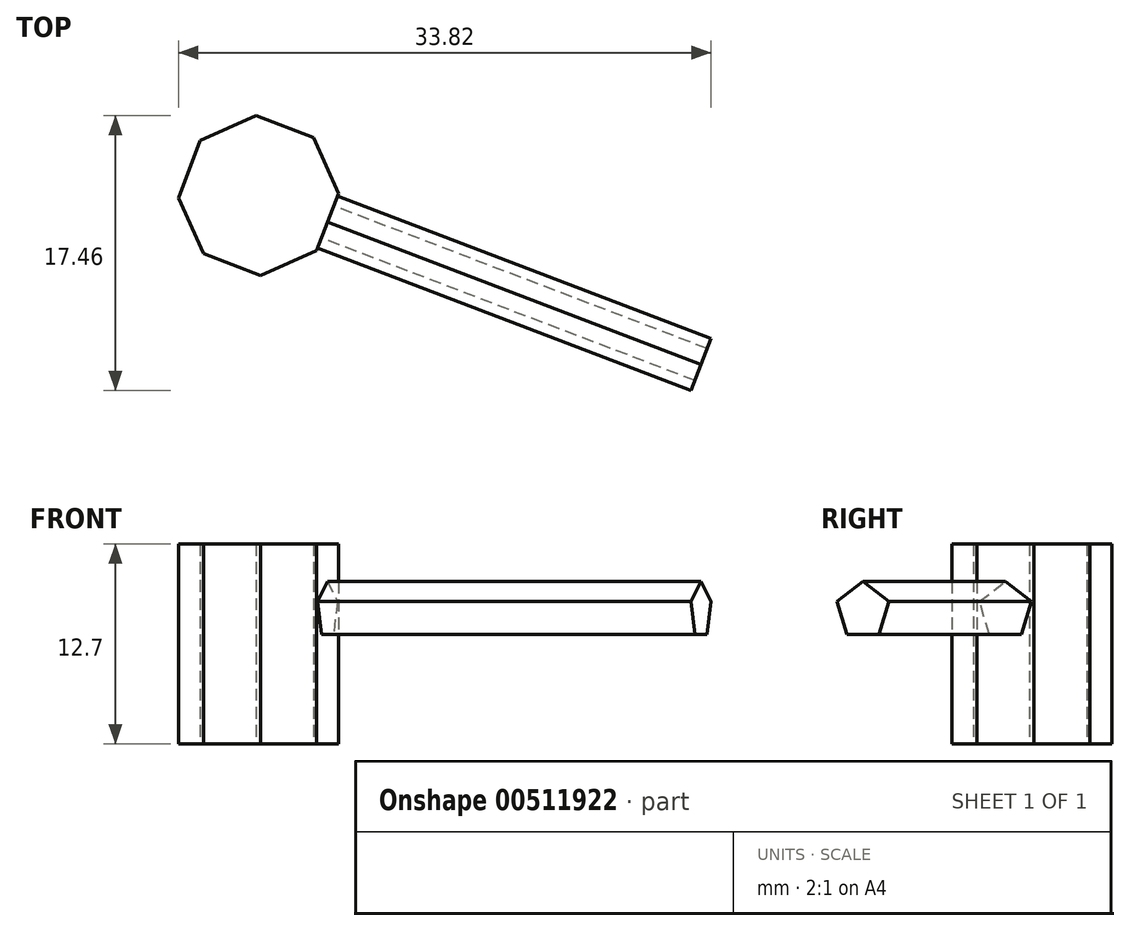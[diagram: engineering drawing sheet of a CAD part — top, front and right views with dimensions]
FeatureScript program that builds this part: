
annotation { "Feature Type Name" : "Feature", "Feature Type Description" : "" }
export const myFeature = defineFeature(function(context is Context, id is Id, definition is map)
    precondition{}
    {
        {
            var Q0;
            Q0=qCreatedBy(makeId("Top.planeOp"),FACE);
            var sketch = newSketch(context, id + "F0", { "sketchPlane" : qUnion([Q0])});
            skCircle(sketch, "E0", {"center": v(0, 0) * mm, "radius": 25.4 * mm});
            skCircle(sketch, "E1.cCircle", {"center": v(0, 0) * mm, "radius": 4.7 * mm, "construction": true});
            skLineSegment(sketch, "E1.0", {"start": v(-3.5, -3.7) * mm, "end": v(-5.08, -0.14) * mm});
            skLineSegment(sketch, "E1.1", {"start": v(-5.08, -0.14) * mm, "end": v(-3.7, 3.5) * mm});
            skLineSegment(sketch, "E1.2", {"start": v(-3.7, 3.5) * mm, "end": v(-0.14, 5.08) * mm});
            skLineSegment(sketch, "E1.3", {"start": v(-0.14, 5.08) * mm, "end": v(3.5, 3.7) * mm});
            skLineSegment(sketch, "E1.4", {"start": v(3.5, 3.7) * mm, "end": v(5.08, 0.14) * mm});
            skLineSegment(sketch, "E1.5", {"start": v(5.08, 0.14) * mm, "end": v(3.7, -3.5) * mm});
            skLineSegment(sketch, "E1.6", {"start": v(3.7, -3.5) * mm, "end": v(0.14, -5.08) * mm});
            skLineSegment(sketch, "E1.7", {"start": v(0.14, -5.08) * mm, "end": v(-3.5, -3.7) * mm});
            skPoint(sketch, "E1.0.midPoint", {"position": v(-4.28, -1.92) * mm});
            skSolve(sketch);
        }
        {
            var Q0;
            Q0=makeQuery(id+"F0.imprint","IMPRINT",FACE,{"disambiguationData":[TD([[makeQuery(id+"F0.imprint","IMPRINT",EDGE,{"derivedFrom":sQuery(id+"F0.wireOp",EDGE,"E1.0")}),-1.0]])]});
            extrude(context, id + "F1", {"entities" : qUnion([Q0]), "depth" : 12.7 * mm});
        }
        {
            var Q0;
            Q0=makeQuery(id+"F1.opExtrude","SWEPT_FACE",FACE,{"disambiguationData":[OSD([sQuery(id+"F0.wireOp",EDGE,"E1.5")])]});
            var sketch = newSketch(context, id + "F2", { "sketchPlane" : qUnion([Q0])});
            skCircle(sketch, "E2.cCircle", {"center": v(0, 8.47) * mm, "radius": 1.5 * mm, "construction": true});
            skLineSegment(sketch, "E2.0", {"start": v(1.1, 6.97) * mm, "end": v(-1.1, 6.97) * mm});
            skLineSegment(sketch, "E2.1", {"start": v(-1.1, 6.97) * mm, "end": v(-1.76, 9.04) * mm});
            skLineSegment(sketch, "E2.2", {"start": v(-1.76, 9.04) * mm, "end": v(0, 10.32) * mm});
            skLineSegment(sketch, "E2.3", {"start": v(0, 10.32) * mm, "end": v(1.76, 9.04) * mm});
            skLineSegment(sketch, "E2.4", {"start": v(1.76, 9.04) * mm, "end": v(1.1, 6.97) * mm});
            skPoint(sketch, "E2.0.midPoint", {"position": v(0, 6.97) * mm});
            skSolve(sketch);
        }
        {
            var Q0;
            Q0=makeQuery(id+"F2.imprint","IMPRINT",FACE,{"disambiguationData":[TD([[makeQuery(id+"F2.imprint","IMPRINT",EDGE,{"derivedFrom":sQuery(id+"F2.wireOp",EDGE,"E2.0")}),-1.0]])]});
            extrude(context, id + "F3", {"entities" : qUnion([Q0]), "operationType" : NewBodyOperationType.ADD, "depth" : 25.4 * mm});
        }
    });
